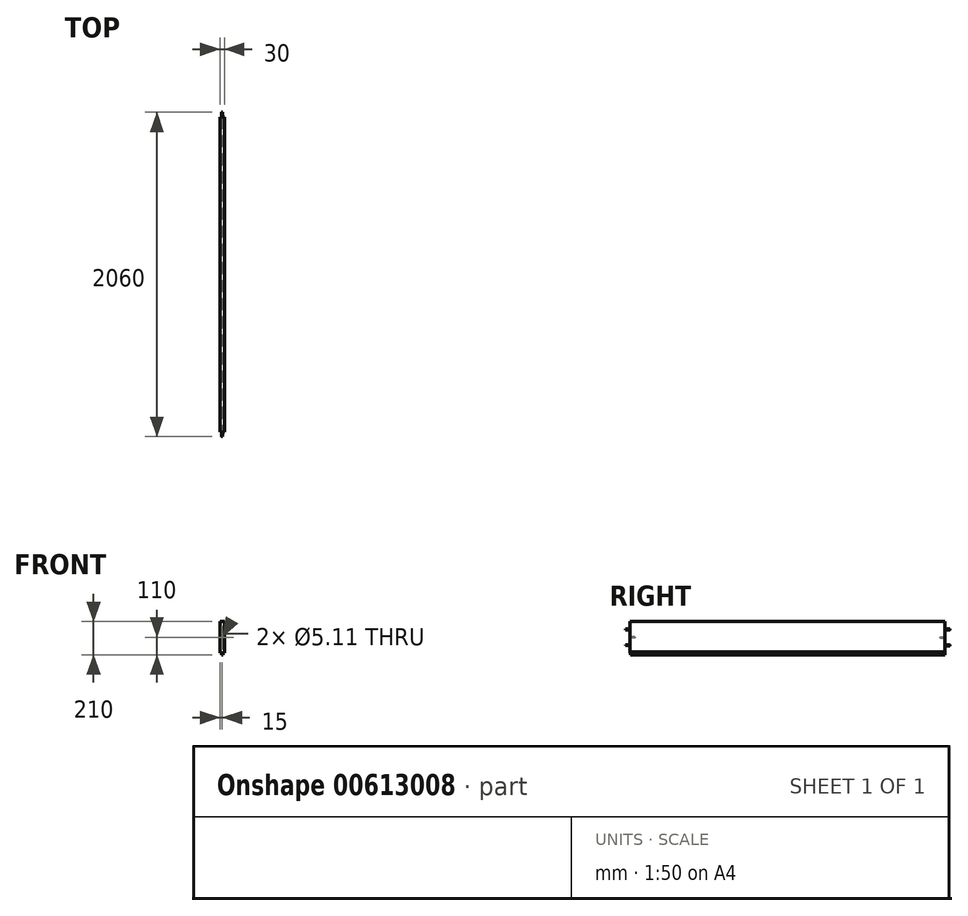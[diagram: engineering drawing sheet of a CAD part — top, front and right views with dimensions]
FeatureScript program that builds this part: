
annotation { "Feature Type Name" : "Feature", "Feature Type Description" : "" }
export const myFeature = defineFeature(function(context is Context, id is Id, definition is map)
    precondition{}
    {
        {
            var Q0;
            Q0=qCreatedBy(makeId("Right.planeOp"),FACE);
            var sketch = newSketch(context, id + "F0", { "sketchPlane" : qUnion([Q0])});
            skLineSegment(sketch, "E0.bottom", {"start": v(1000, -100) * mm, "end": v(-1000, -100) * mm});
            skLineSegment(sketch, "E0.top", {"start": v(1000, 100) * mm, "end": v(-1000, 100) * mm});
            skLineSegment(sketch, "E0.left", {"start": v(1000, -100) * mm, "end": v(1000, 100) * mm});
            skLineSegment(sketch, "E0.right", {"start": v(-1000, -100) * mm, "end": v(-1000, 100) * mm});
            skPoint(sketch, "E0.middle", {"position": v(0, 0) * mm});
            skSolve(sketch);
        }
        {
            var Q0;
            Q0=qSketchRegion(id+"F0",true);
            extrude(context, id + "F1", {"entities" : qUnion([Q0]), "depth" : 30 * mm, "offsetDistance" : 25 * mm});
        }
        {
            var Q0;
            Q0=makeQuery(id+"FdNdVz6oqzI9myz_1.boolean.opBoolean","MERGE",FACE,{"derivedFrom":[makeQuery(id+"FP7T9GCFMjDqVPs_1.boolean.opBoolean","MERGE",FACE,{"derivedFrom":[makeQuery(id+"F1.opExtrude","SWEPT_FACE",FACE,{"disambiguationData":[OSD([sQuery(id+"F0.wireOp",EDGE,"E0.left")])]}),makeQuery(id+"FP7T9GCFMjDqVPs_1.opExtrude","CAP_FACE",FACE,{"disambiguationData":[OSD([sQuery(id+"Fi1JdXIySW0Ez7R_1.wireOp",EDGE,"f0Qjh8i2-KpUz-M0HY-GigP-EJsYWdC2aWoT.bottom"),sQuery(id+"Fi1JdXIySW0Ez7R_1.wireOp",EDGE,"f0Qjh8i2-KpUz-M0HY-GigP-EJsYWdC2aWoT.top"),sQuery(id+"Fi1JdXIySW0Ez7R_1.wireOp",EDGE,"f0Qjh8i2-KpUz-M0HY-GigP-EJsYWdC2aWoT.left"),sQuery(id+"Fi1JdXIySW0Ez7R_1.wireOp",EDGE,"f0Qjh8i2-KpUz-M0HY-GigP-EJsYWdC2aWoT.right")])],"isStart":false})]}),makeQuery(id+"FdNdVz6oqzI9myz_1.opExtrude","CAP_FACE",FACE,{"disambiguationData":[OSD([sQuery(id+"FoLBInOlbBypb1F_1.wireOp",EDGE,"hDGIKLW4-ecLX-UAaE-X4FR-8YsKumgTvVT2.bottom"),sQuery(id+"FoLBInOlbBypb1F_1.wireOp",EDGE,"hDGIKLW4-ecLX-UAaE-X4FR-8YsKumgTvVT2.top"),sQuery(id+"FoLBInOlbBypb1F_1.wireOp",EDGE,"hDGIKLW4-ecLX-UAaE-X4FR-8YsKumgTvVT2.left"),sQuery(id+"FoLBInOlbBypb1F_1.wireOp",EDGE,"hDGIKLW4-ecLX-UAaE-X4FR-8YsKumgTvVT2.right")])],"isStart":false})]});
            var sketch = newSketch(context, id + "F2", { "sketchPlane" : qUnion([Q0])});
            skCircle(sketch, "E1", {"center": v(-15, 50) * mm, "radius": 3 * mm});
            skCircle(sketch, "E2", {"center": v(-15, -50) * mm, "radius": 3 * mm});
            skCircle(sketch, "E3", {"center": v(-15, 0) * mm, "radius": 3 * mm});
            skSolve(sketch);
        }
        {
            var Q0;
            Q0=makeQuery(id+"F2.imprint","IMPRINT",FACE,{"disambiguationData":[TD([[makeQuery(id+"F2.imprint","IMPRINT",EDGE,{"derivedFrom":sQuery(id+"F2.wireOp",EDGE,"E2")}),1.0]])]});
            var Q1;
            Q1=makeQuery(id+"F2.imprint","IMPRINT",FACE,{"disambiguationData":[TD([[makeQuery(id+"F2.imprint","IMPRINT",EDGE,{"derivedFrom":sQuery(id+"F2.wireOp",EDGE,"E1")}),1.0]])]});
            extrude(context, id + "F3", {"entities" : qUnion([Q0, Q1]), "operationType" : NewBodyOperationType.ADD, "depth" : 30 * mm, "offsetDistance" : 25 * mm});
        }
        {
            var Q0;
            Q0=makeQuery(id+"F1.opExtrude","SWEPT_FACE",FACE,{"disambiguationData":[OSD([sQuery(id+"F0.wireOp",EDGE,"E0.right")])]});
            var sketch = newSketch(context, id + "F4", { "sketchPlane" : qUnion([Q0])});
            skLineSegment(sketch, "E4.bottom", {"start": v(20, -110) * mm, "end": v(10, -110) * mm});
            skLineSegment(sketch, "E4.top", {"start": v(20, -100) * mm, "end": v(10, -100) * mm});
            skLineSegment(sketch, "E4.left", {"start": v(20, -110) * mm, "end": v(20, -100) * mm});
            skLineSegment(sketch, "E4.right", {"start": v(10, -110) * mm, "end": v(10, -100) * mm});
            skPoint(sketch, "E4.middle", {"position": v(15, -105) * mm});
            skSolve(sketch);
        }
        {
            var Q0;
            Q0 = qSketchRegion(id + "F4", true);
            extrude(context, id + "F5", {"entities" : qUnion([Q0]), "operationType" : NewBodyOperationType.ADD, "oppositeDirection" : true, "depth" : 1998 * mm, "offsetDistance" : 25 * mm, "hasSecondDirection" : true, "secondDirectionOppositeDirection" : true, "secondDirectionDepth" : 2 * mm});
        }
        {
            var Q0;
            Q0=makeQuery(id+"F5.boolean.opBoolean","MERGE",FACE,{"derivedFrom":[makeQuery(id+"F1.opExtrude","SWEPT_FACE",FACE,{"disambiguationData":[OSD([sQuery(id+"F0.wireOp",EDGE,"E0.right")])]}),makeQuery(id+"F5.opExtrude","CAP_FACE",FACE,{"disambiguationData":[OSD([sQuery(id+"F4.wireOp",EDGE,"E4.bottom"),sQuery(id+"F4.wireOp",EDGE,"E4.top"),sQuery(id+"F4.wireOp",EDGE,"E4.left"),sQuery(id+"F4.wireOp",EDGE,"E4.right")])],"isStart":true})]});
            var sketch = newSketch(context, id + "F6", { "sketchPlane" : qUnion([Q0])});
            skCircle(sketch, "E5", {"center": v(15, 50) * mm, "radius": 3 * mm});
            skCircle(sketch, "E6", {"center": v(15, -50) * mm, "radius": 2.8 * mm});
            skCircle(sketch, "E7", {"center": v(15, 0) * mm, "radius": 3 * mm});
            skSolve(sketch);
        }
        {
            var Q0;
            Q0=makeQuery(id+"F6.imprint","IMPRINT",FACE,{"disambiguationData":[TD([[makeQuery(id+"F6.imprint","IMPRINT",EDGE,{"derivedFrom":sQuery(id+"F6.wireOp",EDGE,"E5")}),1.0]])]});
            var Q1;
            Q1=makeQuery(id+"F6.imprint","IMPRINT",FACE,{"disambiguationData":[TD([[makeQuery(id+"F6.imprint","IMPRINT",EDGE,{"derivedFrom":sQuery(id+"F6.wireOp",EDGE,"E6")}),1.0]])]});
            extrude(context, id + "F7", {"entities" : qUnion([Q0, Q1]), "operationType" : NewBodyOperationType.ADD, "depth" : 30 * mm, "offsetDistance" : 25 * mm});
        }
        {
            var Q0;
            Q0=makeQuery(id+"F5.boolean.opBoolean","MERGE",FACE,{"derivedFrom":[makeQuery(id+"F1.opExtrude","SWEPT_FACE",FACE,{"disambiguationData":[OSD([sQuery(id+"F0.wireOp",EDGE,"E0.right")])]}),makeQuery(id+"F5.opExtrude","CAP_FACE",FACE,{"disambiguationData":[OSD([sQuery(id+"F4.wireOp",EDGE,"E4.bottom"),sQuery(id+"F4.wireOp",EDGE,"E4.top"),sQuery(id+"F4.wireOp",EDGE,"E4.left"),sQuery(id+"F4.wireOp",EDGE,"E4.right")])],"isStart":true})]});
            var sketch = newSketch(context, id + "F8", { "sketchPlane" : qUnion([Q0])});
            skLineSegment(sketch, "E8.bottom", {"start": v(30, -95) * mm, "end": v(20, -95) * mm});
            skLineSegment(sketch, "E8.top", {"start": v(30, -94) * mm, "end": v(20, -94) * mm});
            skLineSegment(sketch, "E8.left", {"start": v(30, -95) * mm, "end": v(30, -94) * mm});
            skLineSegment(sketch, "E8.right", {"start": v(20, -95) * mm, "end": v(20, -94) * mm});
            skPoint(sketch, "E8.middle", {"position": v(25, -94.5) * mm});
            skSolve(sketch);
        }
        {
            var Q0;
            Q0 = qSketchRegion(id + "F8", true);
            extrude(context, id + "F9", {"entities" : qUnion([Q0]), "operationType" : NewBodyOperationType.REMOVE, "oppositeDirection" : true, "depth" : 2000 * mm, "offsetDistance" : 25 * mm});
        }
        {
            var Q0;
            Q0=sQuery(id+"F2.wireOp",VERTEX,"E3.center");
            var Q1;
            Q1=makeQuery(id+"F1.opExtrude","SWEPT_BODY",BODY,{"disambiguationData":[OSD([sQuery(id+"F0.wireOp",EDGE,"E0.bottom"),sQuery(id+"F0.wireOp",EDGE,"E0.top"),sQuery(id+"F0.wireOp",EDGE,"E0.left"),sQuery(id+"F0.wireOp",EDGE,"E0.right")])]});
            hole(context, id + "F10", {"style" : HoleStyle.SIMPLE, "endStyle" : HoleEndStyle.BLIND, "standardTappedOrClearance" : lookupTablePath({ "standard" : "ANSI", "engagement" : "75%", "pitch" : "20 tpi", "size" : "1/4", "type" : "Tapped" }), "standardBlindInLast" : lookupTablePath({ "standard" : "ANSI", "engagement" : "75%", "pitch" : "20 tpi", "size" : "1/4", "type" : "Tapped" }), "holeDiameter" : 5.1 * mm, "majorDiameter" : 6.35 * mm, "showTappedDepth" : true, "holeDepth" : 30 * mm, "isTappedThrough" : true, "tappedDepth" : 26.2 * mm, "tapClearance" : 3, "locations" : qUnion([Q0]), "scope" : qUnion([Q1])});
        }
        {
            var Q0;
            Q0=sQuery(id+"F6.wireOp",VERTEX,"E7.center");
            var Q1;
            Q1=makeQuery(id+"F1.opExtrude","SWEPT_BODY",BODY,{"disambiguationData":[OSD([sQuery(id+"F0.wireOp",EDGE,"E0.bottom"),sQuery(id+"F0.wireOp",EDGE,"E0.top"),sQuery(id+"F0.wireOp",EDGE,"E0.left"),sQuery(id+"F0.wireOp",EDGE,"E0.right")])]});
            hole(context, id + "F11", {"style" : HoleStyle.SIMPLE, "endStyle" : HoleEndStyle.BLIND, "standardTappedOrClearance" : lookupTablePath({ "standard" : "ANSI", "engagement" : "75%", "pitch" : "20 tpi", "size" : "1/4", "type" : "Tapped" }), "standardBlindInLast" : lookupTablePath({ "standard" : "ANSI", "engagement" : "75%", "pitch" : "20 tpi", "size" : "1/4", "type" : "Tapped" }), "holeDiameter" : 5.1 * mm, "majorDiameter" : 6.35 * mm, "showTappedDepth" : true, "holeDepth" : 30 * mm, "isTappedThrough" : true, "tappedDepth" : 26.2 * mm, "tapClearance" : 3, "locations" : qUnion([Q0]), "scope" : qUnion([Q1])});
        }
    });
